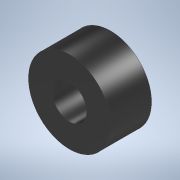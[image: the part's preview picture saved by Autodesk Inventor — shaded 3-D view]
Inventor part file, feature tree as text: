
AUTODESK INVENTOR PART (.ipt)
format: ipt  version: 2020 (Build 240168000, 168)  size: 101,376 bytes
history: native  units: in
note: dims shown in document units (in); Inventor stores cm internally (conversion verified against a paired STEP export)
features: extrude x1, sketch x1
ambient origin geometry x8: Origin, YZ Plane, XZ Plane, XY Plane, X Axis, Y Axis, Z Axis, Center Point
bodies: Solid1 (feature_tree)
feature tree (2):
  extrude  "Extrusion1"  Depth=0.25in
  sketch  "Sketch1"  dims[d0=0.21in d1=0.5in d2=0.25in d3=0.0in]
